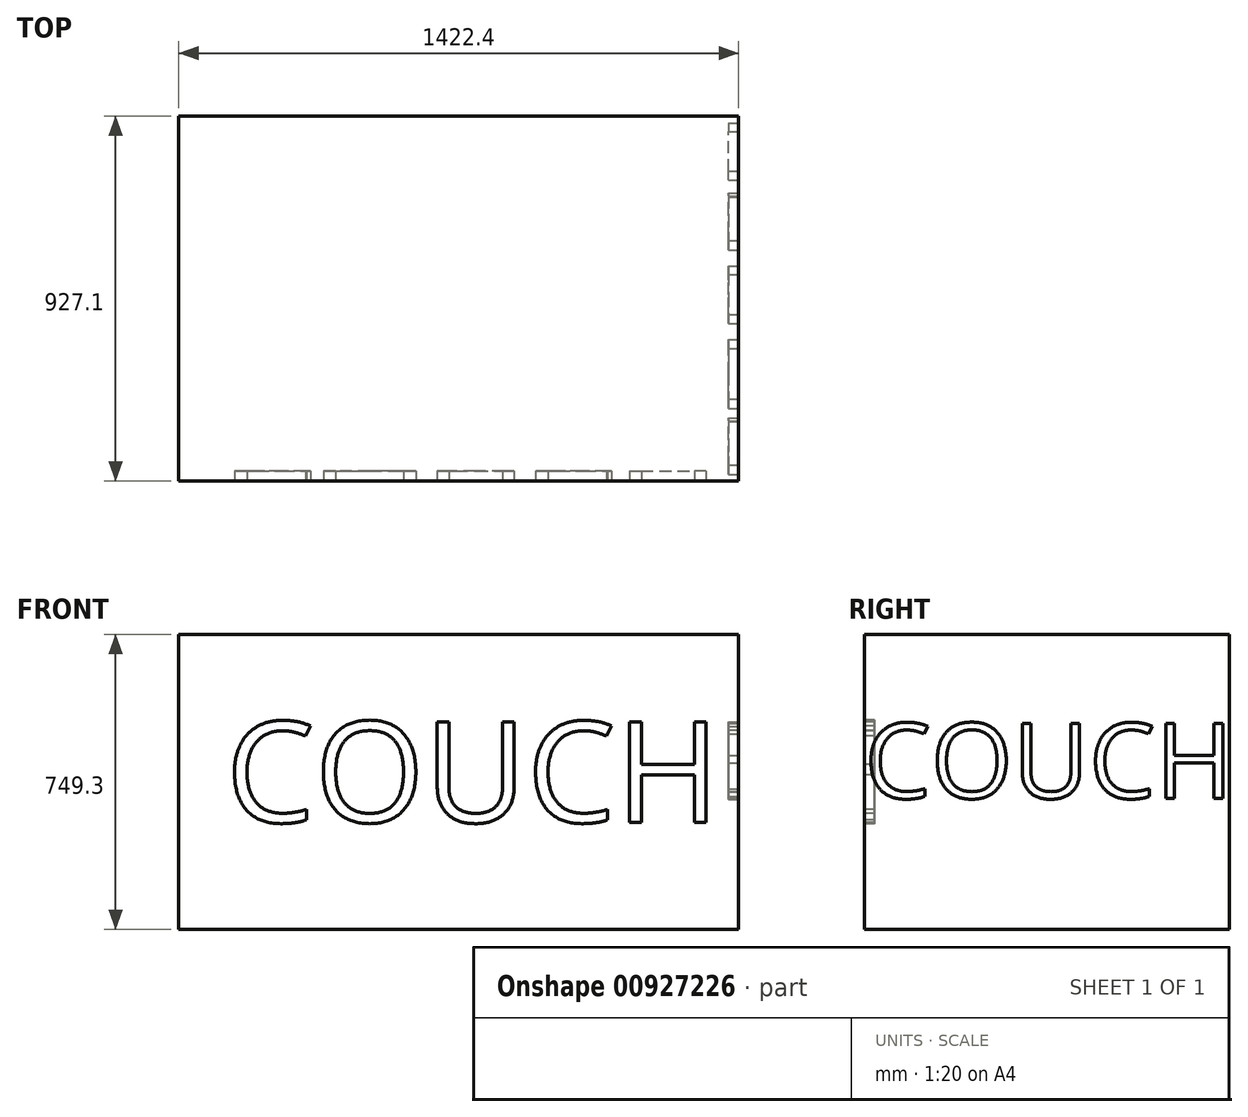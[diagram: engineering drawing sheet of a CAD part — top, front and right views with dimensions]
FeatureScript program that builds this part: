
annotation { "Feature Type Name" : "Feature", "Feature Type Description" : "" }
export const myFeature = defineFeature(function(context is Context, id is Id, definition is map)
    precondition{}
    {
        {
            var Q0;
            Q0=qCreatedBy(makeId("Front.planeOp"),FACE);
            var sketch = newSketch(context, id + "F0", { "sketchPlane" : qUnion([Q0])});
            skLineSegment(sketch, "E0.bottom", {"start": v(711.2, -374.65) * mm, "end": v(-711.2, -374.65) * mm});
            skLineSegment(sketch, "E0.top", {"start": v(711.2, 374.65) * mm, "end": v(-711.2, 374.65) * mm});
            skLineSegment(sketch, "E0.left", {"start": v(711.2, -374.65) * mm, "end": v(711.2, 374.65) * mm});
            skLineSegment(sketch, "E0.right", {"start": v(-711.2, -374.65) * mm, "end": v(-711.2, 374.65) * mm});
            skPoint(sketch, "E0.middle", {"position": v(0, 0) * mm});
            skSolve(sketch);
        }
        {
            var Q0;
            Q0 = qSketchRegion(id + "F0", true);
            extrude(context, id + "F1", {"entities" : qUnion([Q0]), "endBound" : BoundingType.SYMMETRIC, "depth" : 927.1 * mm, "offsetDistance" : 25.4 * mm});
        }
        {
            var Q0;
            Q0=makeQuery(id+"F1.opExtrude","CAP_FACE",FACE,{"disambiguationData":[OSD([sQuery(id+"F0.wireOp",EDGE,"E0.bottom"),sQuery(id+"F0.wireOp",EDGE,"E0.top"),sQuery(id+"F0.wireOp",EDGE,"E0.left"),sQuery(id+"F0.wireOp",EDGE,"E0.right")])],"isStart":false});
            var sketch = newSketch(context, id + "F2", { "sketchPlane" : qUnion([Q0])});
            skText(sketch, "E1", { "text": "COUCH", "fontName": "OpenSans-Regular.ttf"});
            const initialGuessF2  = {"E1": [-0.5913, -0.10248, 1, 0, 0.25762]};
            skSetInitialGuess(sketch, initialGuessF2);
            skSolve(sketch);
        }
        {
            var Q0;
            Q0 = qSketchRegion(id + "F2", true);
            extrude(context, id + "F3", {"entities" : qUnion([Q0]), "operationType" : NewBodyOperationType.REMOVE, "oppositeDirection" : true, "depth" : 25.4 * mm, "offsetDistance" : 25.4 * mm});
        }
        {
            var Q0;
            Q0=makeQuery(id+"F1.opExtrude","SWEPT_FACE",FACE,{"disambiguationData":[OSD([sQuery(id+"F0.wireOp",EDGE,"E0.left")])]});
            var sketch = newSketch(context, id + "F4", { "sketchPlane" : qUnion([Q0])});
            skText(sketch, "E2", { "text": "COUCH", "fontName": "OpenSans-Regular.ttf"});
            const initialGuessF4  = {"E2": [-0.46355, -0.0415, 1, 0, 0.19217]};
            skSetInitialGuess(sketch, initialGuessF4);
            skSolve(sketch);
        }
        {
            var Q0;
            Q0 = qSketchRegion(id + "F4", true);
            extrude(context, id + "F5", {"entities" : qUnion([Q0]), "operationType" : NewBodyOperationType.REMOVE, "oppositeDirection" : true, "depth" : 25.4 * mm, "offsetDistance" : 25.4 * mm});
        }
    });
